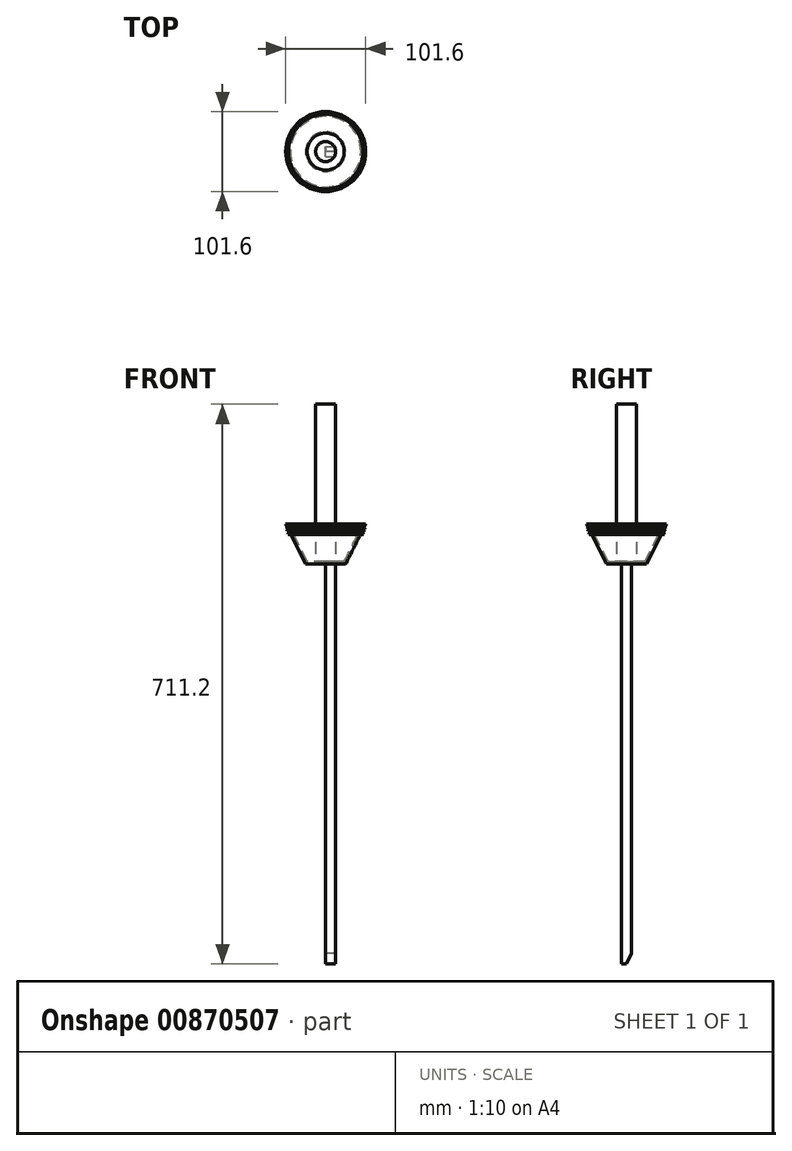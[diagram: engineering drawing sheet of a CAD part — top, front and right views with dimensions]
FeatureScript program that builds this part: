
annotation { "Feature Type Name" : "Feature", "Feature Type Description" : "" }
export const myFeature = defineFeature(function(context is Context, id is Id, definition is map)
    precondition{}
    {
        {
            var Q0;
            Q0=qCreatedBy(makeId("Right.planeOp"),FACE);
            var sketch = newSketch(context, id + "F0", { "sketchPlane" : qUnion([Q0])});
            skLineSegment(sketch, "E0", {"start": v(0, 50.8) * mm, "end": v(0, 0) * mm, "construction": true});
            skLineSegment(sketch, "E1", {"start": v(0, 0) * mm, "end": v(25.4, 0) * mm});
            skLineSegment(sketch, "E2", {"start": v(25.4, 0) * mm, "end": v(50.8, 50.8) * mm});
            skLineSegment(sketch, "E3.0", {"start": v(23.5, 3.07) * mm, "end": v(47.36, 50.8) * mm});
            skLineSegment(sketch, "E3.1", {"start": v(0, 3.07) * mm, "end": v(23.5, 3.07) * mm});
            skLineSegment(sketch, "E4", {"start": v(47.36, 50.8) * mm, "end": v(50.8, 50.8) * mm});
            skLineSegment(sketch, "E5", {"start": v(0, 0) * mm, "end": v(0, 3.07) * mm});
            skLineSegment(sketch, "E6", {"start": v(48.6, 46.4) * mm, "end": v(50.26, 44.36) * mm});
            skLineSegment(sketch, "E7", {"start": v(50.26, 44.36) * mm, "end": v(47.6, 44.16) * mm});
            skLineSegment(sketch, "E8", {"start": v(47.6, 44.16) * mm, "end": v(49.12, 41.17) * mm});
            skLineSegment(sketch, "E9", {"start": v(49.12, 41.17) * mm, "end": v(46.2, 41.55) * mm});
            skLineSegment(sketch, "E10", {"start": v(46.2, 41.55) * mm, "end": v(47.9, 37.57) * mm});
            skLineSegment(sketch, "E11", {"start": v(47.9, 37.57) * mm, "end": v(44.76, 38.76) * mm});
            skSolve(sketch);
        }
        {
            var Q0;
            Q0=makeQuery(id+"F0.imprint","IMPRINT",FACE,{"disambiguationData":[TD([[makeQuery(id+"F0.imprint","IMPRINT",EDGE,{"derivedFrom":sQuery(id+"F0.wireOp",EDGE,"E1")}),1.0]])]});
            var Q1;
            {var subQ0=sQuery(id+"F0.wireOp",EDGE,"E6");Q1=makeQuery(id+"F0.imprint","IMPRINT",FACE,{"disambiguationData":[TD([[makeQuery(id+"F0.imprint","IMPRINT",EDGE,{"derivedFrom":subQ0}),-1.0]])]});}
            var Q2;
            Q2=sQuery(id+"F0.wireOp",EDGE,"E0");
            revolve(context, id + "F1", {"surfaceOperationType" : NewSurfaceOperationType.NEW, "entities" : qUnion([Q0, Q1]), "axis" : qUnion([Q2]), "revolveType" : RevolveType.FULL});
        }
        {
            var Q0;
            Q0=qCreatedBy(makeId("Front.planeOp"),FACE);
            var sketch = newSketch(context, id + "F2", { "sketchPlane" : qUnion([Q0])});
            skLineSegment(sketch, "E12.bottom", {"start": v(0, 0) * mm, "end": v(12.7, 0) * mm});
            skLineSegment(sketch, "E12.top", {"start": v(0, -508) * mm, "end": v(12.7, -508) * mm});
            skLineSegment(sketch, "E12.left", {"start": v(0, 0) * mm, "end": v(0, -508) * mm});
            skLineSegment(sketch, "E12.right", {"start": v(12.7, 0) * mm, "end": v(12.7, -508) * mm});
            skSolve(sketch);
        }
        {
            var Q0;
            Q0 = qSketchRegion(id + "F2", true);
            extrude(context, id + "F3", {"entities" : qUnion([Q0]), "operationType" : NewBodyOperationType.ADD, "endBound" : BoundingType.SYMMETRIC, "depth" : 12.7 * mm, "offsetDistance" : 25.4 * mm});
        }
        {
            var Q0;
            Q0=makeQuery(id+"F3.opExtrude","SWEPT_FACE",FACE,{"disambiguationData":[OSD([sQuery(id+"F2.wireOp",EDGE,"E12.left")])]});
            var sketch = newSketch(context, id + "F4", { "sketchPlane" : qUnion([Q0])});
            skLineSegment(sketch, "E13", {"start": v(0, -508) * mm, "end": v(6.35, -494.38) * mm});
            skLineSegment(sketch, "E14", {"start": v(6.35, -494.38) * mm, "end": v(0, -508) * mm});
            skLineSegment(sketch, "E15", {"start": v(-6.35, -494.38) * mm, "end": v(0, -508) * mm});
            skSolve(sketch);
        }
        {
            var Q0;
            {var subQ0=sQuery(id+"F4.wireOp",EDGE,"E14");Q0=makeQuery(id+"F4.imprint","IMPRINT",FACE,{"disambiguationData":[TD([[makeQuery(id+"F4.imprint","IMPRINT",EDGE,{"derivedFrom":subQ0}),1.0]])]});}
            var Q1;
            {var subQ0=sQuery(id+"F4.wireOp",EDGE,"E15");Q1=makeQuery(id+"F4.imprint","IMPRINT",FACE,{"disambiguationData":[TD([[makeQuery(id+"F4.imprint","IMPRINT",EDGE,{"derivedFrom":subQ0}),-1.0]])]});}
            extrude(context, id + "F5", {"entities" : qUnion([Q0, Q1]), "operationType" : NewBodyOperationType.REMOVE, "oppositeDirection" : true, "depth" : 25.4 * mm, "offsetDistance" : 25.4 * mm});
        }
        {
            var Q0;
            Q0=qCreatedBy(makeId("Front.planeOp"),FACE);
            var sketch = newSketch(context, id + "F6", { "sketchPlane" : qUnion([Q0])});
            skLineSegment(sketch, "E16", {"start": v(0, 0) * mm, "end": v(0, 203.2) * mm});
            skLineSegment(sketch, "E17", {"start": v(12.7, 0) * mm, "end": v(12.7, 203.2) * mm});
            skLineSegment(sketch, "E18", {"start": v(0, 0) * mm, "end": v(12.7, 0) * mm});
            skLineSegment(sketch, "E19", {"start": v(0, 203.2) * mm, "end": v(12.7, 203.2) * mm});
            skSolve(sketch);
        }
        {
            var Q0;
            Q0=makeQuery(id+"F6.imprint","IMPRINT",FACE,{"disambiguationData":[TD([[makeQuery(id+"F6.imprint","IMPRINT",EDGE,{"derivedFrom":sQuery(id+"F6.wireOp",EDGE,"E16")}),-1.0]])]});
            var Q1;
            Q1=sQuery(id+"F6.wireOp",EDGE,"E16");
            revolve(context, id + "F7", {"surfaceOperationType" : NewSurfaceOperationType.NEW, "entities" : qUnion([Q0]), "axis" : qUnion([Q1]), "revolveType" : RevolveType.FULL});
        }
        {
            var Q0;
            Q0 = qSketchRegion(id + "F6", true);
            var Q1;
            Q1=sQuery(id+"F6.wireOp",EDGE,"E16");
            revolve(context, id + "F8", {"operationType" : NewBodyOperationType.ADD, "surfaceOperationType" : NewSurfaceOperationType.NEW, "entities" : qUnion([Q0]), "axis" : qUnion([Q1]), "revolveType" : RevolveType.FULL});
        }
    });
